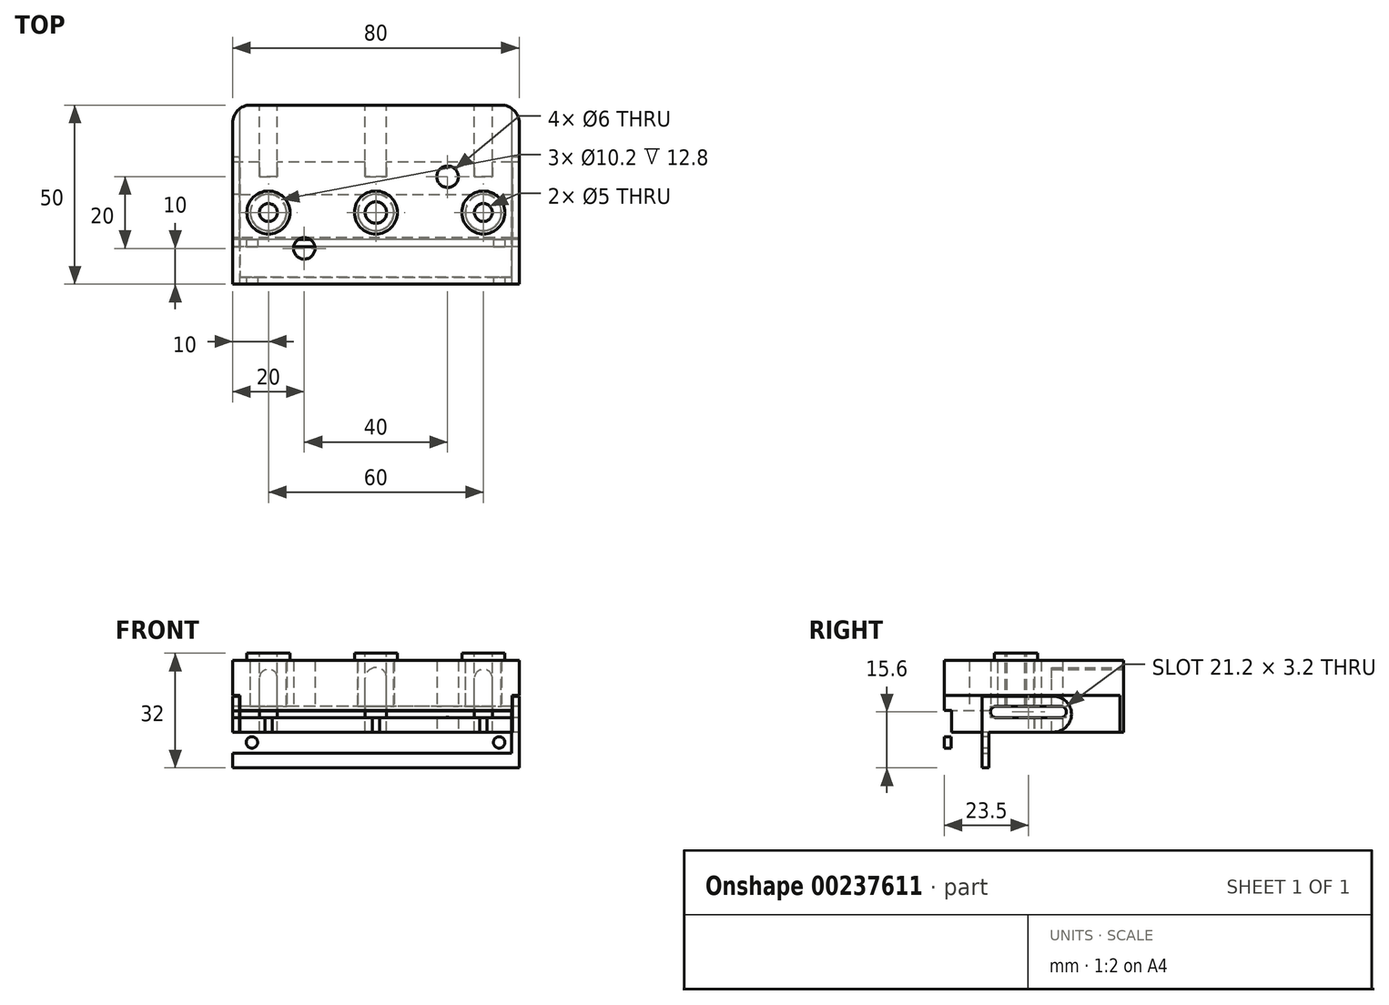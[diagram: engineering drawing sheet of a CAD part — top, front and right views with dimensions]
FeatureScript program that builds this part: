
annotation { "Feature Type Name" : "Feature", "Feature Type Description" : "" }
export const myFeature = defineFeature(function(context is Context, id is Id, definition is map)
    precondition{}
    {
        {
            var Q0;
            Q0=qCreatedBy(makeId("Top.planeOp"),FACE);
            var sketch = newSketch(context, id + "F0", { "sketchPlane" : qUnion([Q0])});
            skLineSegment(sketch, "E0.bottom", {"start": v(40, -25) * mm, "end": v(-40, -25) * mm});
            skLineSegment(sketch, "E0.top", {"start": v(40, 25) * mm, "end": v(-40, 25) * mm});
            skLineSegment(sketch, "E0.left", {"start": v(40, -25) * mm, "end": v(40, 25) * mm});
            skLineSegment(sketch, "E0.right", {"start": v(-40, -25) * mm, "end": v(-40, 25) * mm});
            skPoint(sketch, "E0.middle", {"position": v(0, 0) * mm});
            skLineSegment(sketch, "E1", {"start": v(-40, -5) * mm, "end": v(40, -5) * mm, "construction": true});
            skCircle(sketch, "E2", {"center": v(0, -5) * mm, "radius": 3 * mm});
            skCircle(sketch, "E3", {"center": v(-30, -5) * mm, "radius": 2.5 * mm});
            skCircle(sketch, "E4", {"center": v(30, -5) * mm, "radius": 2.5 * mm});
            skCircle(sketch, "E5", {"center": v(-30, -5) * mm, "radius": 5.1 * mm});
            skCircle(sketch, "E6", {"center": v(0, -5) * mm, "radius": 5.1 * mm});
            skCircle(sketch, "E7", {"center": v(30, -5) * mm, "radius": 5.1 * mm});
            skCircle(sketch, "E8", {"center": v(-20, -15) * mm, "radius": 3 * mm});
            skCircle(sketch, "E9", {"center": v(20, 5) * mm, "radius": 3 * mm});
            skSolve(sketch);
        }
        {
            var Q0;
            Q0 = qSketchRegion(id + "F0", true);
            extrude(context, id + "F1", {"entities" : qUnion([Q0]), "depth" : 20 * mm});
        }
        {
            var Q0;
            Q0=makeQuery(id+"F1.opExtrude","SWEPT_FACE",FACE,{"disambiguationData":[OSD([sQuery(id+"F0.wireOp",EDGE,"E0.top")])]});
            var sketch = newSketch(context, id + "F2", { "sketchPlane" : qUnion([Q0])});
            skLineSegment(sketch, "E10.bottom", {"start": v(3, -15) * mm, "end": v(-3, -15) * mm});
            skLineSegment(sketch, "E10.top", {"start": v(3, 15) * mm, "end": v(-3, 15) * mm});
            skLineSegment(sketch, "E10.left", {"start": v(3, -15) * mm, "end": v(3, 15) * mm});
            skLineSegment(sketch, "E10.right", {"start": v(-3, -15) * mm, "end": v(-3, 15) * mm});
            skPoint(sketch, "E10.middle", {"position": v(0, 0) * mm});
            skCircle(sketch, "E11", {"center": v(0, 15) * mm, "radius": 3 * mm});
            skLineSegment(sketch, "E12.bottom", {"start": v(-27.5, -15) * mm, "end": v(-32.5, -15) * mm});
            skLineSegment(sketch, "E12.top", {"start": v(-27.5, 15) * mm, "end": v(-32.5, 15) * mm});
            skLineSegment(sketch, "E12.left", {"start": v(-27.5, -15) * mm, "end": v(-27.5, 15) * mm});
            skLineSegment(sketch, "E12.right", {"start": v(-32.5, -15) * mm, "end": v(-32.5, 15) * mm});
            skPoint(sketch, "E12.middle", {"position": v(-30, 0) * mm});
            skLineSegment(sketch, "E13.bottom", {"start": v(32.5, -15) * mm, "end": v(27.5, -15) * mm});
            skLineSegment(sketch, "E13.top", {"start": v(32.5, 15) * mm, "end": v(27.5, 15) * mm});
            skLineSegment(sketch, "E13.left", {"start": v(32.5, -15) * mm, "end": v(32.5, 15) * mm});
            skLineSegment(sketch, "E13.right", {"start": v(27.5, -15) * mm, "end": v(27.5, 15) * mm});
            skPoint(sketch, "E13.middle", {"position": v(30, 0) * mm});
            skCircle(sketch, "E14", {"center": v(-30, 15) * mm, "radius": 2.5 * mm});
            skCircle(sketch, "E15", {"center": v(30, 15) * mm, "radius": 2.5 * mm});
            skSolve(sketch);
        }
        {
            var Q0;
            {var subQ0=sQuery(id+"F2.wireOp",EDGE,"E10.top");Q0=makeQuery(id+"F2.imprint","IMPRINT",FACE,{"disambiguationData":[TD([[makeQuery(id+"F2.imprint","IMPRINT",EDGE,{"derivedFrom":subQ0}),-1.0]])]});}
            var Q1;
            {var subQ0=sQuery(id+"F2.wireOp",EDGE,"E10.top");Q1=makeQuery(id+"F2.imprint","IMPRINT",FACE,{"disambiguationData":[TD([[makeQuery(id+"F2.imprint","IMPRINT",EDGE,{"derivedFrom":subQ0}),1.0]])]});}
            var Q2;
            {var subQ0=sQuery(id+"F2.wireOp",EDGE,"E12.top");Q2=makeQuery(id+"F2.imprint","IMPRINT",FACE,{"disambiguationData":[TD([[makeQuery(id+"F2.imprint","IMPRINT",EDGE,{"derivedFrom":subQ0}),-1.0]])]});}
            var Q3;
            {var subQ0=sQuery(id+"F2.wireOp",EDGE,"E12.top");Q3=makeQuery(id+"F2.imprint","IMPRINT",FACE,{"disambiguationData":[TD([[makeQuery(id+"F2.imprint","IMPRINT",EDGE,{"derivedFrom":subQ0}),1.0]])]});}
            var Q4;
            {var subQ0=sQuery(id+"F2.wireOp",EDGE,"E13.top");Q4=makeQuery(id+"F2.imprint","IMPRINT",FACE,{"disambiguationData":[TD([[makeQuery(id+"F2.imprint","IMPRINT",EDGE,{"derivedFrom":subQ0}),-1.0]])]});}
            var Q5;
            {var subQ0=sQuery(id+"F2.wireOp",EDGE,"E13.top");Q5=makeQuery(id+"F2.imprint","IMPRINT",FACE,{"disambiguationData":[TD([[makeQuery(id+"F2.imprint","IMPRINT",EDGE,{"derivedFrom":subQ0}),1.0]])]});}
            var Q6;
            {var subQ1=sQuery(id+"F2.wireOp",EDGE,"E10.left");var subQ4=makeQuery(id+"F1.opExtrude","CAP_EDGE",EDGE,{"disambiguationData":[OSD([sQuery(id+"F0.wireOp",EDGE,"E0.top")])],"isStart":true});var subQ5=makeQuery(id+"F2.imprint","INTERSECT",VERTEX,{"derivedFrom":[subQ4,subQ1]});Q6=makeQuery(id+"F2.imprint","IMPRINT",FACE,{"disambiguationData":[TD([[makeQuery(id+"F2.imprint","IMPRINT",EDGE,{"disambiguationData":[TD([[subQ5,1.0]])],"derivedFrom":subQ4}),1.0]])]});}
            var Q7;
            {var subQ1=sQuery(id+"F2.wireOp",EDGE,"E12.left");var subQ4=makeQuery(id+"F1.opExtrude","CAP_EDGE",EDGE,{"disambiguationData":[OSD([sQuery(id+"F0.wireOp",EDGE,"E0.top")])],"isStart":true});var subQ5=makeQuery(id+"F2.imprint","INTERSECT",VERTEX,{"derivedFrom":[subQ4,subQ1]});Q7=makeQuery(id+"F2.imprint","IMPRINT",FACE,{"disambiguationData":[TD([[makeQuery(id+"F2.imprint","IMPRINT",EDGE,{"disambiguationData":[TD([[subQ5,1.0]])],"derivedFrom":subQ4}),1.0]])]});}
            var Q8;
            {var subQ1=sQuery(id+"F2.wireOp",EDGE,"E13.left");var subQ4=makeQuery(id+"F1.opExtrude","CAP_EDGE",EDGE,{"disambiguationData":[OSD([sQuery(id+"F0.wireOp",EDGE,"E0.top")])],"isStart":true});var subQ5=makeQuery(id+"F2.imprint","INTERSECT",VERTEX,{"derivedFrom":[subQ4,subQ1]});Q8=makeQuery(id+"F2.imprint","IMPRINT",FACE,{"disambiguationData":[TD([[makeQuery(id+"F2.imprint","IMPRINT",EDGE,{"disambiguationData":[TD([[subQ5,1.0]])],"derivedFrom":subQ4}),1.0]])]});}
            extrude(context, id + "F3", {"entities" : qUnion([Q0, Q1, Q2, Q3, Q4, Q5, Q6, Q7, Q8]), "operationType" : NewBodyOperationType.REMOVE, "oppositeDirection" : true, "depth" : 20 * mm});
        }
        {
            var Q0;
            Q0=makeQuery(id+"F1.opExtrude","CAP_FACE",FACE,{"disambiguationData":[OSD([sQuery(id+"F0.wireOp",EDGE,"E0.bottom"),sQuery(id+"F0.wireOp",EDGE,"E0.top"),sQuery(id+"F0.wireOp",EDGE,"E0.left"),sQuery(id+"F0.wireOp",EDGE,"E0.right"),sQuery(id+"F0.wireOp",EDGE,"E5"),sQuery(id+"F0.wireOp",EDGE,"E6"),sQuery(id+"F0.wireOp",EDGE,"E7")])],"isStart":false});
            var sketch = newSketch(context, id + "F4", { "sketchPlane" : qUnion([Q0])});
            skCircle(sketch, "E16", {"center": v(-30, -5) * mm, "radius": 2.5 * mm});
            skCircle(sketch, "E17", {"center": v(0, -5) * mm, "radius": 3 * mm});
            skCircle(sketch, "E18", {"center": v(30, -5) * mm, "radius": 2.5 * mm});
            skCircle(sketch, "E19", {"center": v(-30, -5) * mm, "radius": 5 * mm});
            skCircle(sketch, "E20", {"center": v(0, -5) * mm, "radius": 5 * mm});
            skCircle(sketch, "E21", {"center": v(30, -5) * mm, "radius": 5 * mm});
            skSolve(sketch);
        }
        {
            var Q0;
            Q0=makeQuery(id+"F4.imprint","IMPRINT",FACE,{"disambiguationData":[TD([[makeQuery(id+"F4.imprint","IMPRINT",EDGE,{"derivedFrom":sQuery(id+"F4.wireOp",EDGE,"E18")}),-1.0]])]});
            var Q1;
            Q1=makeQuery(id+"F4.imprint","IMPRINT",FACE,{"disambiguationData":[TD([[makeQuery(id+"F4.imprint","IMPRINT",EDGE,{"derivedFrom":sQuery(id+"F4.wireOp",EDGE,"E17")}),-1.0]])]});
            var Q2;
            Q2=makeQuery(id+"F4.imprint","IMPRINT",FACE,{"disambiguationData":[TD([[makeQuery(id+"F4.imprint","IMPRINT",EDGE,{"derivedFrom":sQuery(id+"F4.wireOp",EDGE,"E16")}),-1.0]])]});
            extrude(context, id + "F5", {"entities" : qUnion([Q0, Q1, Q2]), "oppositeDirection" : true, "depth" : 20 * mm, "hasSecondDirection" : true, "secondDirectionOppositeDirection" : false, "secondDirectionDepth" : 2 * mm});
        }
        {
            var Q0;
            Q0=makeQuery(id+"F1.opExtrude","CAP_FACE",FACE,{"disambiguationData":[OSD([sQuery(id+"F0.wireOp",EDGE,"E0.bottom"),sQuery(id+"F0.wireOp",EDGE,"E0.top"),sQuery(id+"F0.wireOp",EDGE,"E0.left"),sQuery(id+"F0.wireOp",EDGE,"E0.right"),sQuery(id+"F0.wireOp",EDGE,"E5"),sQuery(id+"F0.wireOp",EDGE,"E6"),sQuery(id+"F0.wireOp",EDGE,"E7")])],"isStart":false});
            var sketch = newSketch(context, id + "F6", { "sketchPlane" : qUnion([Q0])});
            skCircle(sketch, "E22", {"center": v(-30, -5) * mm, "radius": 6 * mm});
            skCircle(sketch, "E23", {"center": v(0, -5) * mm, "radius": 6 * mm});
            skCircle(sketch, "E24", {"center": v(30, -5) * mm, "radius": 6 * mm});
            skCircle(sketch, "E25", {"center": v(-30, -5) * mm, "radius": 3.95 * mm});
            skCircle(sketch, "E26", {"center": v(0, -5) * mm, "radius": 4.25 * mm});
            skCircle(sketch, "E27", {"center": v(30, -5) * mm, "radius": 4.39 * mm});
            skSolve(sketch);
        }
        {
            var Q0;
            Q0=makeQuery(id+"F6.imprint","IMPRINT",FACE,{"disambiguationData":[TD([[makeQuery(id+"F6.imprint","IMPRINT",EDGE,{"derivedFrom":sQuery(id+"F6.wireOp",EDGE,"E23")}),1.0]])]});
            var Q1;
            Q1=makeQuery(id+"F6.imprint","IMPRINT",FACE,{"disambiguationData":[TD([[makeQuery(id+"F6.imprint","IMPRINT",EDGE,{"derivedFrom":sQuery(id+"F6.wireOp",EDGE,"E22")}),1.0]])]});
            var Q2;
            Q2=makeQuery(id+"F6.imprint","IMPRINT",FACE,{"disambiguationData":[TD([[makeQuery(id+"F6.imprint","IMPRINT",EDGE,{"derivedFrom":sQuery(id+"F6.wireOp",EDGE,"E24")}),1.0]])]});
            var Q3;
            Q3=makeQuery(id+"F6.imprint","IMPRINT",FACE,{"disambiguationData":[TD([[makeQuery(id+"F6.imprint","IMPRINT",EDGE,{"derivedFrom":sQuery(id+"F6.wireOp",EDGE,"E25")}),-1.0]])]});
            var Q4;
            Q4=makeQuery(id+"F6.imprint","IMPRINT",FACE,{"disambiguationData":[TD([[makeQuery(id+"F6.imprint","IMPRINT",EDGE,{"derivedFrom":sQuery(id+"F6.wireOp",EDGE,"E26")}),-1.0]])]});
            var Q5;
            Q5=makeQuery(id+"F6.imprint","IMPRINT",FACE,{"disambiguationData":[TD([[makeQuery(id+"F6.imprint","IMPRINT",EDGE,{"derivedFrom":sQuery(id+"F6.wireOp",EDGE,"E27")}),-1.0]])]});
            extrude(context, id + "F7", {"entities" : qUnion([Q0, Q1, Q2, Q3, Q4, Q5]), "operationType" : NewBodyOperationType.ADD, "depth" : 2 * mm});
        }
        {
            var Q0;
            Q0=makeQuery(id+"F1.opExtrude","CAP_FACE",FACE,{"disambiguationData":[OSD([sQuery(id+"F0.wireOp",EDGE,"E0.bottom"),sQuery(id+"F0.wireOp",EDGE,"E0.top"),sQuery(id+"F0.wireOp",EDGE,"E0.left"),sQuery(id+"F0.wireOp",EDGE,"E0.right"),sQuery(id+"F0.wireOp",EDGE,"E5"),sQuery(id+"F0.wireOp",EDGE,"E6"),sQuery(id+"F0.wireOp",EDGE,"E7")])],"isStart":true});
            var sketch = newSketch(context, id + "F8", { "sketchPlane" : qUnion([Q0])});
            skLineSegment(sketch, "E28.bottom", {"start": v(40, 14.5) * mm, "end": v(-40, 14.5) * mm});
            skLineSegment(sketch, "E28.top", {"start": v(40, 12.5) * mm, "end": v(-40, 12.5) * mm});
            skLineSegment(sketch, "E28.left", {"start": v(40, 14.5) * mm, "end": v(40, 12.5) * mm});
            skLineSegment(sketch, "E28.right", {"start": v(-40, 14.5) * mm, "end": v(-40, 12.5) * mm});
            skPoint(sketch, "E28.middle", {"position": v(0, 13.5) * mm});
            skLineSegment(sketch, "E29", {"start": v(0, 5) * mm, "end": v(-5.1, 5) * mm, "construction": true});
            skSolve(sketch);
        }
        {
            var Q0;
            Q0 = qSketchRegion(id + "F8", true);
            extrude(context, id + "F9", {"entities" : qUnion([Q0]), "depth" : 10 * mm});
        }
        {
            var Q0;
            Q0=makeQuery(id+"F1.opExtrude","CAP_FACE",FACE,{"disambiguationData":[OSD([sQuery(id+"F0.wireOp",EDGE,"E0.bottom"),sQuery(id+"F0.wireOp",EDGE,"E0.top"),sQuery(id+"F0.wireOp",EDGE,"E0.left"),sQuery(id+"F0.wireOp",EDGE,"E0.right"),sQuery(id+"F0.wireOp",EDGE,"E5"),sQuery(id+"F0.wireOp",EDGE,"E6"),sQuery(id+"F0.wireOp",EDGE,"E7")])],"isStart":true});
            var sketch = newSketch(context, id + "F10", { "sketchPlane" : qUnion([Q0])});
            skLineSegment(sketch, "E30.bottom", {"start": v(-40, 25) * mm, "end": v(-38, 25) * mm});
            skLineSegment(sketch, "E30.top", {"start": v(-40, -25) * mm, "end": v(-38, -25) * mm});
            skLineSegment(sketch, "E30.left", {"start": v(-40, 25) * mm, "end": v(-40, -25) * mm});
            skLineSegment(sketch, "E30.right", {"start": v(-38, 25) * mm, "end": v(-38, -25) * mm});
            skLineSegment(sketch, "E31.bottom", {"start": v(40, 25) * mm, "end": v(38, 25) * mm});
            skLineSegment(sketch, "E31.top", {"start": v(40, -25) * mm, "end": v(38, -25) * mm});
            skLineSegment(sketch, "E31.left", {"start": v(40, 25) * mm, "end": v(40, -25) * mm});
            skLineSegment(sketch, "E31.right", {"start": v(38, 25) * mm, "end": v(38, -25) * mm});
            skSolve(sketch);
        }
        {
            var Q0;
            Q0 = qSketchRegion(id + "F10", true);
            extrude(context, id + "F11", {"entities" : qUnion([Q0]), "operationType" : NewBodyOperationType.REMOVE, "oppositeDirection" : true, "depth" : 10.2 * mm});
        }
        {
            var Q0;
            Q0=makeQuery(id+"F1.opExtrude","CAP_FACE",FACE,{"disambiguationData":[OSD([sQuery(id+"F0.wireOp",EDGE,"E0.bottom"),sQuery(id+"F0.wireOp",EDGE,"E0.top"),sQuery(id+"F0.wireOp",EDGE,"E0.left"),sQuery(id+"F0.wireOp",EDGE,"E0.right"),sQuery(id+"F0.wireOp",EDGE,"E5"),sQuery(id+"F0.wireOp",EDGE,"E6"),sQuery(id+"F0.wireOp",EDGE,"E7")])],"isStart":true});
            var sketch = newSketch(context, id + "F12", { "sketchPlane" : qUnion([Q0])});
            skLineSegment(sketch, "E32.bottom", {"start": v(-40, 14.5) * mm, "end": v(-38.1, 14.5) * mm});
            skLineSegment(sketch, "E32.top", {"start": v(-40, -10.5) * mm, "end": v(-38.1, -10.5) * mm});
            skLineSegment(sketch, "E32.left", {"start": v(-40, 14.5) * mm, "end": v(-40, -10.5) * mm});
            skLineSegment(sketch, "E32.right", {"start": v(-38.1, 14.5) * mm, "end": v(-38.1, -10.5) * mm});
            skLineSegment(sketch, "E33.MirrorCS", {"start": v(40, 14.5) * mm, "end": v(40, -10.5) * mm});
            skLineSegment(sketch, "E34.MirrorCS", {"start": v(40, -10.5) * mm, "end": v(38.1, -10.5) * mm});
            skLineSegment(sketch, "E35.MirrorCS", {"start": v(38.1, 14.5) * mm, "end": v(38.1, -10.5) * mm});
            skLineSegment(sketch, "E36.MirrorCS", {"start": v(40, 14.5) * mm, "end": v(38.1, 14.5) * mm});
            skSolve(sketch);
        }
        {
            var Q0;
            Q0 = qSketchRegion(id + "F12", true);
            extrude(context, id + "F13", {"entities" : qUnion([Q0]), "operationType" : NewBodyOperationType.ADD, "oppositeDirection" : true, "depth" : 10 * mm});
        }
        {
            var Q0;
            Q0=makeQuery(id+"F13.boolean.opBoolean","MERGE",FACE,{"derivedFrom":[makeQuery(id+"F9.opExtrude","SWEPT_FACE",FACE,{"disambiguationData":[OSD([sQuery(id+"F8.wireOp",EDGE,"E28.right")])]}),makeQuery(id+"F13.opExtrude","SWEPT_FACE",FACE,{"disambiguationData":[OSD([sQuery(id+"F12.wireOp",EDGE,"E32.left")])]})]});
            var sketch = newSketch(context, id + "F14", { "sketchPlane" : qUnion([Q0])});
            skLineSegment(sketch, "E37.bottom", {"start": v(-7.5, 7.2) * mm, "end": v(10.5, 7.2) * mm});
            skLineSegment(sketch, "E37.top", {"start": v(-7.5, 4) * mm, "end": v(10.5, 4) * mm});
            skLineSegment(sketch, "E37.left", {"start": v(-7.5, 7.2) * mm, "end": v(-7.5, 4) * mm});
            skLineSegment(sketch, "E37.right", {"start": v(10.5, 7.2) * mm, "end": v(10.5, 4) * mm});
            skCircle(sketch, "E38", {"center": v(-7.5, 5.6) * mm, "radius": 1.6 * mm});
            skCircle(sketch, "E39", {"center": v(10.5, 5.6) * mm, "radius": 1.6 * mm});
            skSolve(sketch);
        }
        {
            var Q0;
            Q0 = qSketchRegion(id + "F14", true);
            extrude(context, id + "F15", {"entities" : qUnion([Q0]), "operationType" : NewBodyOperationType.REMOVE, "oppositeDirection" : true, "depth" : 90 * mm});
        }
        {
            var Q0;
            Q0=makeQuery(id+"F13.opExtrude","CAP_EDGE",EDGE,{"disambiguationData":[OSD([sQuery(id+"F12.wireOp",EDGE,"E32.top")])],"isStart":false});
            var Q1;
            Q1=makeQuery(id+"F13.opExtrude","CAP_EDGE",EDGE,{"disambiguationData":[OSD([sQuery(id+"F12.wireOp",EDGE,"E32.top")])],"isStart":true});
            var Q2;
            Q2=makeQuery(id+"F13.opExtrude","CAP_EDGE",EDGE,{"disambiguationData":[OSD([sQuery(id+"F12.wireOp",EDGE,"E34.MirrorCS")])],"isStart":false});
            var Q3;
            Q3=makeQuery(id+"F13.opExtrude","CAP_EDGE",EDGE,{"disambiguationData":[OSD([sQuery(id+"F12.wireOp",EDGE,"E34.MirrorCS")])],"isStart":true});
            fillet(context, id + "F16", {"entities" : qUnion([Q0, Q1, Q2, Q3]), "radius" : 5 * mm, "tangentPropagation" : true, "allowEdgeOverflow" : false});
        }
        {
            var Q0;
            Q0=makeQuery(id+"F11.boolean.opBoolean","COPY",FACE,{"derivedFrom":makeQuery(id+"F11.opExtrude","SWEPT_FACE",FACE,{"disambiguationData":[OSD([sQuery(id+"F10.wireOp",EDGE,"E30.right")])]})});
            var sketch = newSketch(context, id + "F17", { "sketchPlane" : qUnion([Q0])});
            skCircle(sketch, "E40", {"center": v(5, 5.6) * mm, "radius": 1.4 * mm});
            skSolve(sketch);
        }
        {
            var Q0;
            Q0=makeQuery(id+"F11.boolean.opBoolean","COPY",FACE,{"derivedFrom":makeQuery(id+"F11.opExtrude","SWEPT_FACE",FACE,{"disambiguationData":[OSD([sQuery(id+"F10.wireOp",EDGE,"E31.right")])]})});
            var sketch = newSketch(context, id + "F18", { "sketchPlane" : qUnion([Q0])});
            skCircle(sketch, "E41", {"center": v(276.45, -88.62) * mm, "radius": 1.4 * mm});
            skCircle(sketch, "E42", {"center": v(-5, 5.6) * mm, "radius": 1.4 * mm});
            skSolve(sketch);
        }
        {
            var Q0;
            Q0=makeQuery(id+"F17.imprint","IMPRINT",FACE,{"disambiguationData":[TD([[makeQuery(id+"F17.imprint","IMPRINT",EDGE,{"derivedFrom":sQuery(id+"F17.wireOp",EDGE,"E40")}),1.0]])]});
            var Q1;
            Q1=makeQuery(id+"F18.imprint","IMPRINT",FACE,{"disambiguationData":[TD([[makeQuery(id+"F18.imprint","IMPRINT",EDGE,{"derivedFrom":sQuery(id+"F18.wireOp",EDGE,"E42")}),1.0]])]});
            extrude(context, id + "F19", {"entities" : qUnion([Q0, Q1]), "operationType" : NewBodyOperationType.REMOVE, "endBound" : BoundingType.SYMMETRIC, "oppositeDirection" : true, "depth" : 5 * mm});
        }
        {
            var Q0;
            Q0=makeQuery(id+"F1.opExtrude","SWEPT_EDGE",EDGE,{"disambiguationData":[OSD([sQuery(id+"F0.wireOp",EDGE,"E0.top"),sQuery(id+"F0.wireOp",EDGE,"E0.right")])]});
            var Q1;
            Q1=makeQuery(id+"F1.opExtrude","SWEPT_EDGE",EDGE,{"disambiguationData":[OSD([sQuery(id+"F0.wireOp",EDGE,"E0.top"),sQuery(id+"F0.wireOp",EDGE,"E0.left")])]});
            fillet(context, id + "F20", {"entities" : qUnion([Q0, Q1]), "radius" : 5 * mm, "tangentPropagation" : true, "allowEdgeOverflow" : false});
        }
        {
            var Q0;
            Q0=makeQuery(id+"F11.boolean.opBoolean","COPY",FACE,{"derivedFrom":makeQuery(id+"F11.opExtrude","SWEPT_FACE",FACE,{"disambiguationData":[OSD([sQuery(id+"F10.wireOp",EDGE,"E30.right")])]})});
            var sketch = newSketch(context, id + "F21", { "sketchPlane" : qUnion([Q0])});
            skLineSegment(sketch, "E43.bottom", {"start": v(25, 0) * mm, "end": v(23, 0) * mm});
            skLineSegment(sketch, "E43.top", {"start": v(25, 6) * mm, "end": v(23, 6) * mm});
            skLineSegment(sketch, "E43.left", {"start": v(25, 0) * mm, "end": v(25, 6) * mm});
            skLineSegment(sketch, "E43.right", {"start": v(23, 0) * mm, "end": v(23, 6) * mm});
            skSolve(sketch);
        }
        {
            var Q0;
            Q0=makeQuery(id+"F21.imprint","IMPRINT",FACE,{"disambiguationData":[TD([[makeQuery(id+"F21.imprint","IMPRINT",EDGE,{"derivedFrom":sQuery(id+"F21.wireOp",EDGE,"E43.bottom")}),-1.0]])]});
            extrude(context, id + "F22", {"entities" : qUnion([Q0]), "operationType" : NewBodyOperationType.REMOVE, "oppositeDirection" : true, "depth" : 80 * mm});
        }
        {
            var Q0;
            Q0=makeQuery(id+"F13.boolean.opBoolean","MERGE",FACE,{"derivedFrom":[makeQuery(id+"F9.opExtrude","SWEPT_FACE",FACE,{"disambiguationData":[OSD([sQuery(id+"F8.wireOp",EDGE,"E28.right")])]}),makeQuery(id+"F13.opExtrude","SWEPT_FACE",FACE,{"disambiguationData":[OSD([sQuery(id+"F12.wireOp",EDGE,"E32.left")])]})]});
            var sketch = newSketch(context, id + "F23", { "sketchPlane" : qUnion([Q0])});
            skLineSegment(sketch, "E44.bottom", {"start": v(25, -5.95) * mm, "end": v(0, -5.95) * mm});
            skLineSegment(sketch, "E44.top", {"start": v(25, 5.95) * mm, "end": v(0, 5.95) * mm});
            skLineSegment(sketch, "E44.left", {"start": v(25, -5.95) * mm, "end": v(25, 5.95) * mm});
            skLineSegment(sketch, "E44.right", {"start": v(0, -5.95) * mm, "end": v(0, 5.95) * mm});
            skPoint(sketch, "E44.middle", {"position": v(12.5, 0) * mm});
            skSolve(sketch);
        }
        {
            var Q0;
            {var subQ0=sQuery(id+"F23.wireOp",EDGE,"STliwHdx-aC8F-cw7a-ap9E-4qkPohLZ3l73.top");Q0=makeQuery(id+"F23.imprint","IMPRINT",FACE,{"disambiguationData":[TD([[makeQuery(id+"F23.imprint","IMPRINT",EDGE,{"derivedFrom":subQ0}),-1.0]])]});}
            var Q1;
            {var subQ0=sQuery(id+"F23.wireOp",EDGE,"E44.right");var subQ1=sQuery(id+"F23.wireOp",EDGE,"E44.bottom");var subQ2=makeQuery(id+"F23.imprint","INTERSECT",VERTEX,{"derivedFrom":[subQ1,subQ0]});Q1=makeQuery(id+"F23.imprint","IMPRINT",FACE,{"disambiguationData":[TD([[makeQuery(id+"F23.imprint","IMPRINT",EDGE,{"disambiguationData":[TD([[subQ2,-1.0]])],"derivedFrom":subQ0}),-1.0]])]});}
            var Q2;
            {var subQ0=sQuery(id+"F23.wireOp",EDGE,"E44.left");Q2=makeQuery(id+"F23.imprint","IMPRINT",FACE,{"disambiguationData":[TD([[makeQuery(id+"F23.imprint","IMPRINT",EDGE,{"derivedFrom":subQ0}),1.0]])]});}
            var Q3;
            {var subQ0=sQuery(id+"F12.wireOp",EDGE,"E32.left");var subQ1=makeQuery(id+"F13.opExtrude","CAP_EDGE",EDGE,{"disambiguationData":[OSD([subQ0])],"isStart":true});var subQ13=sQuery(id+"F23.wireOp",EDGE,"E44.right");var subQ14=makeQuery(id+"F23.imprint","INTERSECT",VERTEX,{"derivedFrom":[subQ1,subQ13]});Q3=makeQuery(id+"F23.imprint","IMPRINT",FACE,{"disambiguationData":[TD([[makeQuery(id+"F23.imprint","IMPRINT",EDGE,{"disambiguationData":[TD([[subQ14,-1.0]])],"derivedFrom":subQ13}),-1.0]])]});}
            var Q4;
            {var subQ0=sQuery(id+"F23.wireOp",EDGE,"E44.right");var subQ1=sQuery(id+"F23.wireOp",EDGE,"E44.top");var subQ2=makeQuery(id+"F23.imprint","INTERSECT",VERTEX,{"derivedFrom":[subQ1,subQ0]});Q4=makeQuery(id+"F23.imprint","IMPRINT",FACE,{"disambiguationData":[TD([[makeQuery(id+"F23.imprint","IMPRINT",EDGE,{"disambiguationData":[TD([[subQ2,1.0]])],"derivedFrom":subQ1}),1.0]])]});}
            extrude(context, id + "F24", {"entities" : qUnion([Q0, Q1, Q2, Q3, Q4]), "depth" : 2.1 * mm, "hasSecondDirection" : true, "secondDirectionOppositeDirection" : false, "secondDirectionDepth" : 0.1 * mm});
        }
        {
            var Q0;
            Q0=makeQuery(id+"F24.opExtrude","CAP_FACE",FACE,{"disambiguationData":[OSD([sQuery(id+"F23.wireOp",EDGE,"E44.bottom"),sQuery(id+"F23.wireOp",EDGE,"E44.top"),sQuery(id+"F23.wireOp",EDGE,"E44.left"),sQuery(id+"F23.wireOp",EDGE,"E44.right"),sQuery(id+"F23.wireOp",EDGE,"STliwHdx-aC8F-cw7a-ap9E-4qkPohLZ3l73.top"),sQuery(id+"F23.wireOp",EDGE,"STliwHdx-aC8F-cw7a-ap9E-4qkPohLZ3l73.right")])],"isStart":false});
            var sketch = newSketch(context, id + "F25", { "sketchPlane" : qUnion([Q0])});
            skLineSegment(sketch, "E45.bottom", {"start": v(25, 5.95) * mm, "end": v(23.1, 5.95) * mm});
            skLineSegment(sketch, "E45.top", {"start": v(25, -5.95) * mm, "end": v(23.1, -5.95) * mm});
            skLineSegment(sketch, "E45.left", {"start": v(25, 5.95) * mm, "end": v(25, -5.95) * mm});
            skLineSegment(sketch, "E45.right", {"start": v(23.1, 5.95) * mm, "end": v(23.1, -5.95) * mm});
            skSolve(sketch);
        }
        {
            var Q0;
            Q0 = qSketchRegion(id + "F25", true);
            extrude(context, id + "F26", {"entities" : qUnion([Q0]), "operationType" : NewBodyOperationType.ADD, "oppositeDirection" : true, "depth" : 80 * mm});
        }
        {
            var Q0;
            Q0=makeQuery(id+"F24.opExtrude","CAP_FACE",FACE,{"disambiguationData":[OSD([sQuery(id+"F23.wireOp",EDGE,"E44.bottom"),sQuery(id+"F23.wireOp",EDGE,"E44.top"),sQuery(id+"F23.wireOp",EDGE,"E44.left"),sQuery(id+"F23.wireOp",EDGE,"E44.right")])],"isStart":false});
            var sketch = newSketch(context, id + "F27", { "sketchPlane" : qUnion([Q0])});
            skLineSegment(sketch, "E46.bottom", {"start": v(0, 5.95) * mm, "end": v(9, 5.95) * mm});
            skLineSegment(sketch, "E46.top", {"start": v(0, 2.95) * mm, "end": v(9, 2.95) * mm});
            skLineSegment(sketch, "E46.left", {"start": v(0, 5.95) * mm, "end": v(0, 2.95) * mm});
            skLineSegment(sketch, "E46.right", {"start": v(9, 5.95) * mm, "end": v(9, 2.95) * mm});
            skLineSegment(sketch, "E47.MirrorCS", {"start": v(0, -2.95) * mm, "end": v(9, -2.95) * mm});
            skLineSegment(sketch, "E48.MirrorCS", {"start": v(9, -5.95) * mm, "end": v(9, -2.95) * mm});
            skLineSegment(sketch, "E49.MirrorCS", {"start": v(0, -5.95) * mm, "end": v(9, -5.95) * mm});
            skLineSegment(sketch, "E50.MirrorCS", {"start": v(0, -5.95) * mm, "end": v(0, -2.95) * mm});
            skSolve(sketch);
        }
        {
            var Q0;
            Q0=makeQuery(id+"F27.imprint","IMPRINT",FACE,{"disambiguationData":[TD([[makeQuery(id+"F27.imprint","IMPRINT",EDGE,{"derivedFrom":sQuery(id+"F27.wireOp",EDGE,"E46.bottom")}),1.0]])]});
            var Q1;
            Q1=makeQuery(id+"F27.imprint","IMPRINT",FACE,{"disambiguationData":[TD([[makeQuery(id+"F27.imprint","IMPRINT",EDGE,{"derivedFrom":sQuery(id+"F27.wireOp",EDGE,"E47.MirrorCS")}),-1.0]])]});
            extrude(context, id + "F28", {"entities" : qUnion([Q0, Q1]), "operationType" : NewBodyOperationType.REMOVE, "oppositeDirection" : true, "depth" : 25 * mm});
        }
        {
            var Q0;
            Q0=makeQuery(id+"F28.boolean.opBoolean","COPY",EDGE,{"derivedFrom":makeQuery(id+"F28.opExtrude","SWEPT_EDGE",EDGE,{"disambiguationData":[OSD([sQuery(id+"F27.wireOp",EDGE,"E46.top"),sQuery(id+"F27.wireOp",EDGE,"E46.right")])]})});
            var Q1;
            Q1=makeQuery(id+"F28.boolean.opBoolean","COPY",EDGE,{"derivedFrom":makeQuery(id+"F28.opExtrude","SWEPT_EDGE",EDGE,{"disambiguationData":[OSD([sQuery(id+"F27.wireOp",EDGE,"E47.MirrorCS"),sQuery(id+"F27.wireOp",EDGE,"E48.MirrorCS")])]})});
            fillet(context, id + "F29", {"entities" : qUnion([Q0, Q1]), "radius" : 2 * mm, "tangentPropagation" : true, "allowEdgeOverflow" : false});
        }
        {
            var Q0;
            Q0=makeQuery(id+"F26.boolean.opBoolean","MERGE",FACE,{"derivedFrom":[makeQuery(id+"F24.opExtrude","SWEPT_FACE",FACE,{"disambiguationData":[OSD([sQuery(id+"F23.wireOp",EDGE,"E44.left")])]}),makeQuery(id+"F26.opExtrude","SWEPT_FACE",FACE,{"disambiguationData":[OSD([sQuery(id+"F25.wireOp",EDGE,"E45.left")])]})]});
            var sketch = newSketch(context, id + "F30", { "sketchPlane" : qUnion([Q0])});
            skLineSegment(sketch, "E51.bottom", {"start": v(-34.6, 4.5) * mm, "end": v(34.4, 4.5) * mm});
            skLineSegment(sketch, "E51.top", {"start": v(-34.6, 1.3) * mm, "end": v(34.4, 1.3) * mm});
            skLineSegment(sketch, "E51.left", {"start": v(-34.6, 4.5) * mm, "end": v(-34.6, 1.3) * mm});
            skLineSegment(sketch, "E51.right", {"start": v(34.4, 4.5) * mm, "end": v(34.4, 1.3) * mm});
            skCircle(sketch, "E52", {"center": v(34.4, 2.9) * mm, "radius": 1.6 * mm});
            skCircle(sketch, "E53", {"center": v(-34.6, 2.9) * mm, "radius": 1.6 * mm});
            skLineSegment(sketch, "E54.MirrorCS", {"start": v(-34.6, -1.3) * mm, "end": v(34.4, -1.3) * mm});
            skLineSegment(sketch, "E55.MirrorCS", {"start": v(-34.6, -4.5) * mm, "end": v(34.4, -4.5) * mm});
            skCircle(sketch, "E56.MirrorC", {"center": v(-34.6, -2.9) * mm, "radius": 1.6 * mm});
            skCircle(sketch, "E57.MirrorC", {"center": v(34.4, -2.9) * mm, "radius": 1.6 * mm});
            skSolve(sketch);
        }
        {
            var Q0;
            {var subQ0=sQuery(id+"F30.wireOp",EDGE,"E51.bottom");Q0=makeQuery(id+"F30.imprint","IMPRINT",FACE,{"disambiguationData":[TD([[makeQuery(id+"F30.imprint","IMPRINT",EDGE,{"derivedFrom":subQ0}),-1.0]])]});}
            var Q1;
            {var subQ0=sQuery(id+"F30.wireOp",EDGE,"E51.left");Q1=makeQuery(id+"F30.imprint","IMPRINT",FACE,{"disambiguationData":[TD([[makeQuery(id+"F30.imprint","IMPRINT",EDGE,{"derivedFrom":subQ0}),1.0]])]});}
            var Q2;
            {var subQ0=sQuery(id+"F30.wireOp",EDGE,"E51.left");Q2=makeQuery(id+"F30.imprint","IMPRINT",FACE,{"disambiguationData":[TD([[makeQuery(id+"F30.imprint","IMPRINT",EDGE,{"derivedFrom":subQ0}),-1.0]])]});}
            var Q3;
            {var subQ0=sQuery(id+"F30.wireOp",EDGE,"E56.MirrorC");var subQ1=makeQuery(id+"F30.imprint","INTERSECT",VERTEX,{"derivedFrom":[sQuery(id+"F30.wireOp",EDGE,"E54.MirrorCS"),subQ0]});Q3=makeQuery(id+"F30.imprint","IMPRINT",FACE,{"disambiguationData":[TD([[makeQuery(id+"F30.imprint","IMPRINT",EDGE,{"disambiguationData":[TD([[subQ1,1.0]])],"derivedFrom":subQ0}),-1.0]])]});}
            var Q4;
            {var subQ0=sQuery(id+"F30.wireOp",EDGE,"E54.MirrorCS");Q4=makeQuery(id+"F30.imprint","IMPRINT",FACE,{"disambiguationData":[TD([[makeQuery(id+"F30.imprint","IMPRINT",EDGE,{"derivedFrom":subQ0}),-1.0]])]});}
            var Q5;
            {var subQ0=sQuery(id+"F30.wireOp",EDGE,"E57.MirrorC");var subQ1=makeQuery(id+"F30.imprint","INTERSECT",VERTEX,{"derivedFrom":[sQuery(id+"F30.wireOp",EDGE,"E54.MirrorCS"),subQ0]});Q5=makeQuery(id+"F30.imprint","IMPRINT",FACE,{"disambiguationData":[TD([[makeQuery(id+"F30.imprint","IMPRINT",EDGE,{"disambiguationData":[TD([[subQ1,1.0]])],"derivedFrom":subQ0}),-1.0]])]});}
            var Q6;
            {var subQ0=sQuery(id+"F30.wireOp",EDGE,"E51.right");Q6=makeQuery(id+"F30.imprint","IMPRINT",FACE,{"disambiguationData":[TD([[makeQuery(id+"F30.imprint","IMPRINT",EDGE,{"derivedFrom":subQ0}),1.0]])]});}
            var Q7;
            {var subQ0=sQuery(id+"F30.wireOp",EDGE,"E51.right");Q7=makeQuery(id+"F30.imprint","IMPRINT",FACE,{"disambiguationData":[TD([[makeQuery(id+"F30.imprint","IMPRINT",EDGE,{"derivedFrom":subQ0}),-1.0]])]});}
            extrude(context, id + "F31", {"entities" : qUnion([Q0, Q1, Q2, Q3, Q4, Q5, Q6, Q7]), "operationType" : NewBodyOperationType.REMOVE, "oppositeDirection" : true, "depth" : 25 * mm});
        }
        {
            var Q0;
            Q0=makeQuery(id+"F22.boolean.opBoolean","COPY",FACE,{"derivedFrom":makeQuery(id+"F22.opExtrude","SWEPT_FACE",FACE,{"disambiguationData":[OSD([sQuery(id+"F21.wireOp",EDGE,"E43.right")])]})});
            var sketch = newSketch(context, id + "F32", { "sketchPlane" : qUnion([Q0])});
            skCircle(sketch, "E58", {"center": v(-32.4, 2.9) * mm, "radius": 1.4 * mm});
            skCircle(sketch, "E59.MirrorC", {"center": v(32.4, 2.9) * mm, "radius": 1.4 * mm});
            skSolve(sketch);
        }
        {
            var Q0;
            Q0 = qSketchRegion(id + "F32", true);
            extrude(context, id + "F33", {"entities" : qUnion([Q0]), "operationType" : NewBodyOperationType.REMOVE, "oppositeDirection" : true, "depth" : 5 * mm});
        }
    });
